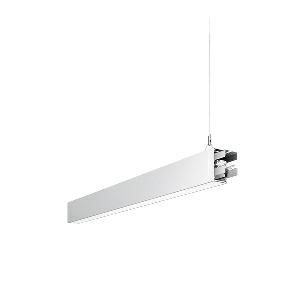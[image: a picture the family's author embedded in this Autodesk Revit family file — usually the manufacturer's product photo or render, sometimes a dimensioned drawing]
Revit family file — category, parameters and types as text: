
# Revit family: idoo_line_-_ilp_2000_840_d_mid_00805681_ff68
name_source: partatom
category: Lighting Fixtures
units: mm (PartAtom-declared; Revit-internal decimal feet)

## family parameters
Cut with Voids When Loaded = No
Host = Face
Light Source = No
Part Type = Normal
Room Calculation Point = No
Round Connector Dimension = Use Diameter
Shared = No

## types (1)
- IDOO.line - ILP 2000/840/D MID (1 x LED, 2350 lm, 4000K)
    Apparent Load = 17 VA
    Approval mark = CE
    CIE Flux Codes = 66 91 98 40 100
    Color Rendering = 80-89
    Color Temperature = 4000K
    Control Gear = Electronic ballast
    Default Elevation = 1800 mm
    Description = ILP 2000/840/D|Suspended luminaire|light source: LED|connected load: 220-240 V, 50/60 Hz|Power consumption: approx. 17 W|standby: approx. 0,20|luminous flux: 2350 lm|luminous efficacy: 138 lm/W|light distribution: Direct/indirect|direct ratio: approx. 40 %|colour temperature: Cold white, ca. 4000 K|color rendering index (CRI): >= 80|chromaticity tolerance:  3 SDCM|System of protection: IP 40|technology: Continuously dimmable|luminaire body|material: Sectional aluminium|colour: White|lamp cover: Acrylic (PMMA), Clear|mains lead: 1,0 m With free stranded wires|Fastening: Steel cable 0.3 - 0.7 m|glare control: Prism aperture|luminance(L65): <= 2700 cd/m|unified glare rating(4H 8H): <=  16|special features: DALI Load 1x, TouchDIM - dimming via standard switch, Through-wired, up to 18 m on one mains connection, Flicker-free, Suitable as emergency lighting, Mechanical and electrical connection of the individual modules without tools|
    Frequency = 50 Hz
    Height = 110 mm
    Lamp = 1 x LED
    Lamp Light Flux = 2350 lm
    Lamp count = 1
    Length = 842 mm
    Luminous efficacy = 138 lm/W
    Manufacturer = Waldmann
    ModVariant = No
    Model = 00805681
    Mounting Place = Ceiling
    Mounting Type = Pendant
    Number of Poles = 1
    OnlyDefault = Yes
    Power Factor = 1
    Product Name = IDOO.line - ILP 2000/840/D MID
    Product group = Suspended luminaire
    ProductGroupID = 9
    Protection Class = Protection class I
    Protection Degree = IP 40
    RLX_Detail_Level = 1
    RLX_Emergency_Light_Flux = 0 lm
    RLX_Emergency_Type = 0
    RLX_Emergency_Type_DB = No
    RlxData = <blob elided: 17909 chars, md5=7105daa4>
    Socket = socket
    Standby Power = 0 W
    System Light Flux = 2350 lm
    System Power = 17 W
    Type Comments = Product without accessories
    Type Image = 113296000-00692546.jpg
    URL = http://relux.com
    VarID = ---
    Voltage = 230 V
    Voltage Range = 220-240 V
    Weight = 0.00 kg
    Width = 60 mm  [stored 0.19685 ft]

note: [stored X ft] marks values corroborated as IEEE doubles in the binary element streams (Revit-internal decimal feet)

## geometry (parser evidence)
native form markers: Blend x4, Sweep x13
no freeform markers — native parametric forms only
